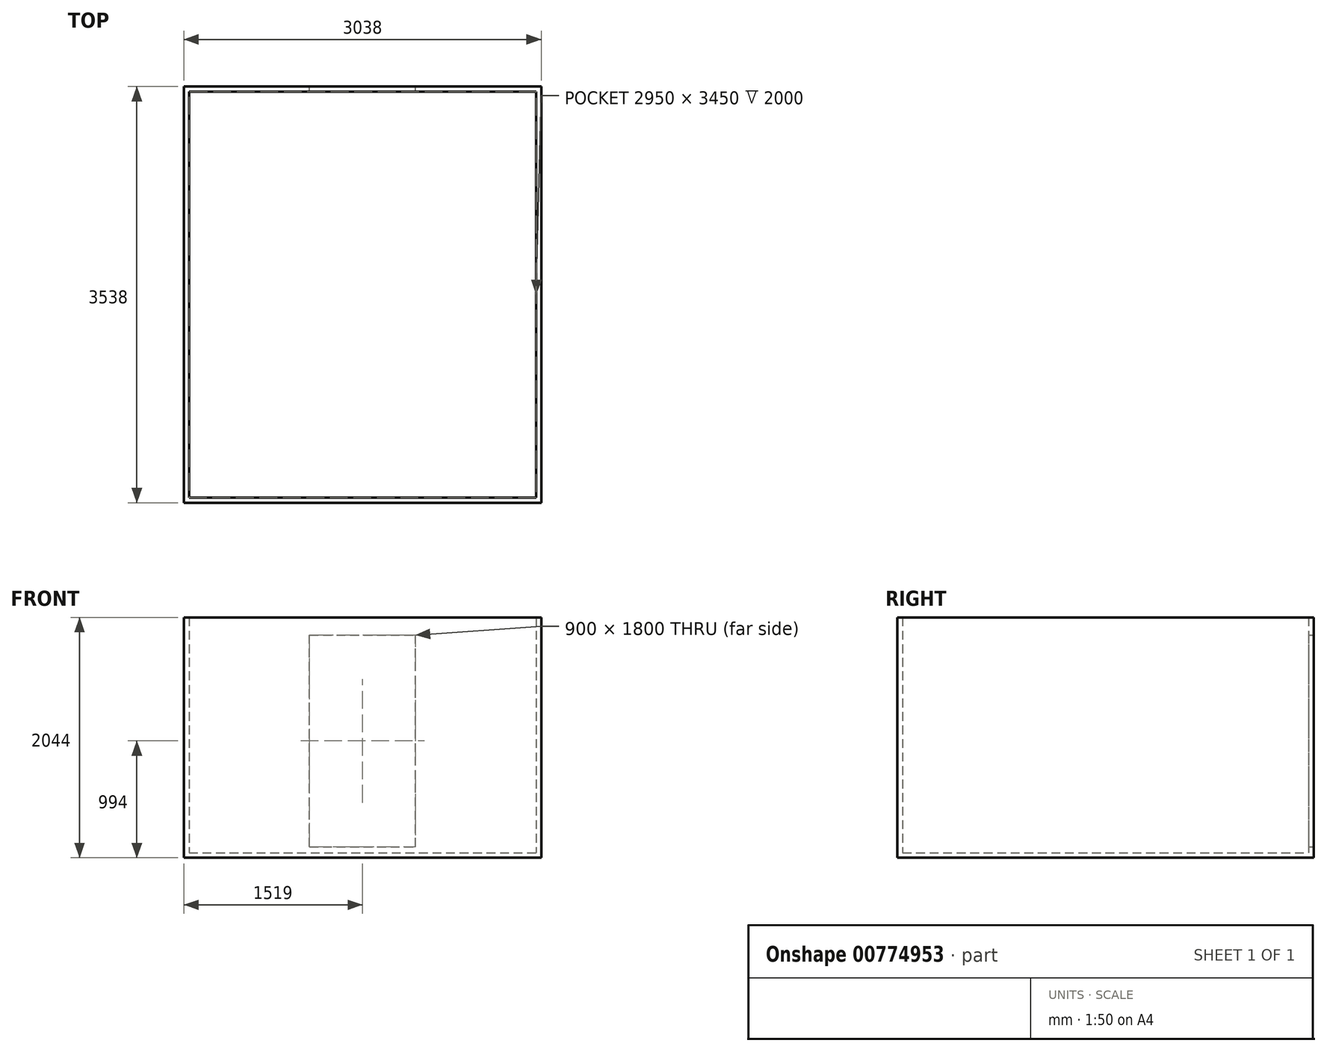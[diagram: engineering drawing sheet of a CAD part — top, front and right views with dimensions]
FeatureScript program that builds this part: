
annotation { "Feature Type Name" : "Feature", "Feature Type Description" : "" }
export const myFeature = defineFeature(function(context is Context, id is Id, definition is map)
    precondition{}
    {
        {
            var Q0;
            Q0=qCreatedBy(makeId("Top.planeOp"),FACE);
            var sketch = newSketch(context, id + "F0", { "sketchPlane" : qUnion([Q0])});
            skLineSegment(sketch, "E0.bottom", {"start": v(-1475, -1725) * mm, "end": v(1475, -1725) * mm});
            skLineSegment(sketch, "E0.top", {"start": v(-1475, 1725) * mm, "end": v(1475, 1725) * mm});
            skLineSegment(sketch, "E0.left", {"start": v(-1475, -1725) * mm, "end": v(-1475, 1725) * mm});
            skLineSegment(sketch, "E0.right", {"start": v(1475, -1725) * mm, "end": v(1475, 1725) * mm});
            skPoint(sketch, "E0.middle", {"position": v(0, 0) * mm});
            skSolve(sketch);
        }
        {
            var Q0;
            Q0=makeQuery(id+"F0.imprint","IMPRINT",FACE,{"disambiguationData":[TD([[makeQuery(id+"F0.imprint","IMPRINT",EDGE,{"derivedFrom":sQuery(id+"F0.wireOp",EDGE,"E0.bottom")}),1.0]])]});
            extrude(context, id + "F1", {"entities" : qUnion([Q0]), "depth" : 2000 * mm, "offsetDistance" : 25 * mm});
        }
        {
            var Q0;
            Q0=makeQuery(id+"F1.opExtrude","CAP_FACE",FACE,{"disambiguationData":[OSD([sQuery(id+"F0.wireOp",EDGE,"E0.bottom"),sQuery(id+"F0.wireOp",EDGE,"E0.top"),sQuery(id+"F0.wireOp",EDGE,"E0.left"),sQuery(id+"F0.wireOp",EDGE,"E0.right")])],"isStart":false});
            shell(context, id + "F2", {"entities" : qUnion([Q0]), "thickness" : 44 * mm, "oppositeDirection" : true});
        }
        {
            var Q0;
            Q0=makeQuery(id+"F1.opExtrude","SWEPT_FACE",FACE,{"disambiguationData":[OSD([sQuery(id+"F0.wireOp",EDGE,"E0.top")])]});
            var sketch = newSketch(context, id + "F3", { "sketchPlane" : qUnion([Q0])});
            skLineSegment(sketch, "E1.bottom", {"start": v(450, 50) * mm, "end": v(-450, 50) * mm});
            skLineSegment(sketch, "E1.top", {"start": v(450, 1850) * mm, "end": v(-450, 1850) * mm});
            skLineSegment(sketch, "E1.left", {"start": v(450, 50) * mm, "end": v(450, 1850) * mm});
            skLineSegment(sketch, "E1.right", {"start": v(-450, 50) * mm, "end": v(-450, 1850) * mm});
            skPoint(sketch, "E1.middle", {"position": v(0, 950) * mm});
            skSolve(sketch);
        }
        {
            var Q0;
            Q0=makeQuery(id+"F3.imprint","IMPRINT",FACE,{"disambiguationData":[TD([[makeQuery(id+"F3.imprint","IMPRINT",EDGE,{"derivedFrom":sQuery(id+"F3.wireOp",EDGE,"E1.bottom")}),-1.0]])]});
            extrude(context, id + "F4", {"entities" : qUnion([Q0]), "operationType" : NewBodyOperationType.REMOVE, "endBound" : BoundingType.UP_TO_NEXT, "oppositeDirection" : true, "depth" : 25 * mm, "offsetDistance" : 25 * mm});
        }
        {
            var Q0;
            Q0=makeQuery(id+"F1.opExtrude","SWEPT_FACE",FACE,{"disambiguationData":[OSD([sQuery(id+"F0.wireOp",EDGE,"E0.bottom")])]});
            var sketch = newSketch(context, id + "F5", { "sketchPlane" : qUnion([Q0])});
            skFitSpline(sketch, "E2", {"points": [v(974.66, 2201.64) * mm, v(608.86, 792) * mm, v(-2357.1, 379.93) * mm], "startDerivative": vector(-39.04, -3992.09) * mm, "endDerivative": vector(-6255.1, 105.18) * mm});
            skLineSegment(sketch, "E3", {"start": v(-2357.1, 379.93) * mm, "end": v(-2357.1, 2201.64) * mm});
            skLineSegment(sketch, "E4", {"start": v(-2357.1, 2201.64) * mm, "end": v(974.66, 2201.64) * mm});
            skSolve(sketch);
        }
        {
            var Q0;
            Q0=makeQuery(id+"F2.opShell","OFFSET_FACE",FACE,{"disambiguationData":[OSD([sQuery(id+"F0.wireOp",EDGE,"E0.bottom"),sQuery(id+"F0.wireOp",EDGE,"E0.top"),sQuery(id+"F0.wireOp",EDGE,"E0.left"),sQuery(id+"F0.wireOp",EDGE,"E0.right")])]});
            cPlane(context, id + "F6", {"entities" : qUnion([Q0]), "cplaneType" : CPlaneType.OFFSET, "offset" : 1200 * mm, "width" : 150 * mm, "height" : 150 * mm});
        }
    });
